# Revit family: Accessory-Cabinet_Knob-KOHLER-Shea_McGee-K-29979-1
name_source: partatom
category: Specialty Equipment
units: mm (PartAtom-declared; Revit-internal decimal feet)

## family parameters
Cut with Voids When Loaded = No
Host = Face
Maintain Annotation Orientation = No
OmniClass Number = 23.21.19.17.13
OmniClass Title = Casework Component Hardware
Part Type = Normal
Room Calculation Point = No
Round Connector Dimension = Use Diameter
Shared = No

## types (6) — shared parameters
ADA Compliant = No
Assembly Code = C1030200
Date Modified = 03/27/2025
Default Elevation = 42"
Description = Cabinet Knob
Height = 1 1/8"
Length = 1 1/8"
Manufacturer = Kohler Co.
Master Format 2014 = 10 28 00
Master Format 2014 Name = Toilet, Bath, and Laundry Accessories
Material = Premium Metal Construction
Product Documentation Link = https://www.us.kohler.com
Product Name = Shea McGee
Product Page URL = http://www.us.kohler.com
URL = https://www.us.kohler.com
WaterSense Certified = No
Width = 1 1/16"

## per-type parameters (varying)
| type | Finish | Model | Type |
| 2MB-Vibrant Brushed Moderne Brass | Kohler-Metal-2MB-Vibrant_Brushed_Moderne_Brass | K-29979-2MB | 1 |
| BL-Matte Black | Kohler-Metal-BL-Matte_Black | K-29979-BL | 2 |
| BN-Vibrant Brushed Nickel | Kohler-Metal-BN-Vibrant_Brushed_Nickel | K-29979-BN | 3 |
| CP-Polished Chrome | Kohler-Metal-CP-Polished_Chrome | K-29979-CP | 4 |
| SN-Vibrant Polished Nickel | Kohler-Metal-SN-Vibrant_Polished_Nickel | K-29979-SN | 5 |
| DR-Deep Bronze | Kohler-Metal-DR-Deep_Bronze | K-29979-DR | 6 |

## geometry (parser evidence)
native form markers: Sweep x5
no freeform markers — native parametric forms only
